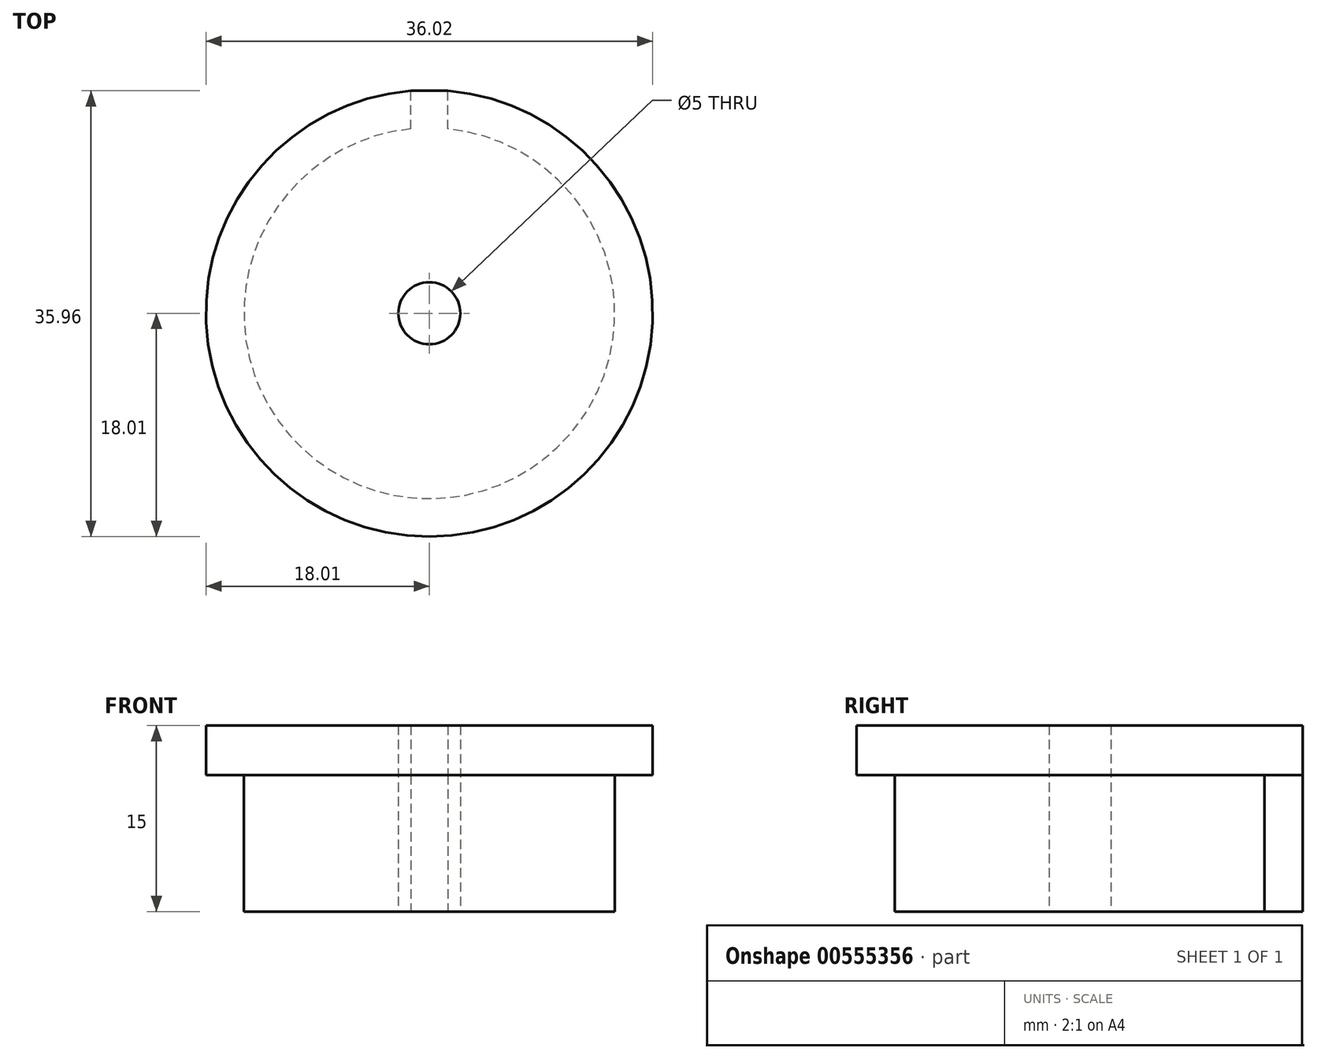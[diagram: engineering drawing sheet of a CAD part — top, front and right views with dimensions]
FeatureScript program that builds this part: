
annotation { "Feature Type Name" : "Feature", "Feature Type Description" : "" }
export const myFeature = defineFeature(function(context is Context, id is Id, definition is map)
    precondition{}
    {
        {
            var Q0;
            Q0=qCreatedBy(makeId("Top.planeOp"),FACE);
            var sketch = newSketch(context, id + "F0", { "sketchPlane" : qUnion([Q0])});
            skArc(sketch, "E0", {"start": v(-1.5, 14.87) * mm, "mid": v(0, -14.95) * mm, "end": v(1.5, 14.87) * mm});
            skLineSegment(sketch, "E1.top", {"start": v(1.5, 17.95) * mm, "end": v(-1.5, 17.95) * mm});
            skLineSegment(sketch, "E1.left", {"start": v(1.5, 14.87) * mm, "end": v(1.5, 17.95) * mm});
            skLineSegment(sketch, "E1.right", {"start": v(-1.5, 14.87) * mm, "end": v(-1.5, 17.95) * mm});
            skPoint(sketch, "E1.middle", {"position": v(0, 14.95) * mm});
            skPoint(sketch, "E2.orphan", {"position": v(-1.5, 11.95) * mm});
            skPoint(sketch, "E3.orphan", {"position": v(1.5, 11.95) * mm});
            skSolve(sketch);
        }
        {
            var Q0;
            Q0=qSketchRegion(id+"F0",true);
            extrude(context, id + "F1", {"entities" : qUnion([Q0]), "depth" : 11 * mm, "offsetDistance" : 25 * mm});
        }
        {
            var Q0;
            Q0=makeQuery(id+"F1.opExtrude","CAP_FACE",FACE,{"disambiguationData":[OSD([sQuery(id+"F0.wireOp",EDGE,"E0"),sQuery(id+"F0.wireOp",EDGE,"E1.top"),sQuery(id+"F0.wireOp",EDGE,"E1.left"),sQuery(id+"F0.wireOp",EDGE,"E1.right")])],"isStart":false});
            var sketch = newSketch(context, id + "F2", { "sketchPlane" : qUnion([Q0])});
            skCircle(sketch, "E4", {"center": v(0, 0) * mm, "radius": 18.01 * mm});
            skSolve(sketch);
        }
        {
            var Q0;
            Q0=makeQuery(id+"F2.imprint","IMPRINT",FACE,{"disambiguationData":[TD([[makeQuery(id+"F2.imprint","IMPRINT",EDGE,{"derivedFrom":makeQuery(id+"F1.opExtrude","CAP_EDGE",EDGE,{"disambiguationData":[OSD([sQuery(id+"F0.wireOp",EDGE,"E0")])],"isStart":false})}),-1.0]])]});
            var Q1;
            Q1=makeQuery(id+"F2.imprint","IMPRINT",FACE,{"disambiguationData":[TD([[makeQuery(id+"F2.imprint","IMPRINT",EDGE,{"derivedFrom":makeQuery(id+"F1.opExtrude","CAP_EDGE",EDGE,{"disambiguationData":[OSD([sQuery(id+"F0.wireOp",EDGE,"E0")])],"isStart":false})}),1.0]])]});
            extrude(context, id + "F3", {"entities" : qUnion([Q0, Q1]), "operationType" : NewBodyOperationType.ADD, "depth" : 4 * mm, "offsetDistance" : 25 * mm});
        }
        {
            var Q0;
            Q0=makeQuery(id+"F1.opExtrude","CAP_FACE",FACE,{"disambiguationData":[OSD([sQuery(id+"F0.wireOp",EDGE,"E0"),sQuery(id+"F0.wireOp",EDGE,"E1.top"),sQuery(id+"F0.wireOp",EDGE,"E1.left"),sQuery(id+"F0.wireOp",EDGE,"E1.right")])],"isStart":true});
            var sketch = newSketch(context, id + "F4", { "sketchPlane" : qUnion([Q0])});
            skPoint(sketch, "E5", {"position": v(0, 0) * mm});
            skSolve(sketch);
        }
        {
            var Q0;
            Q0=sQuery(id+"F4.wireOp",VERTEX,"E5");
            var Q1;
            Q1=makeQuery(id+"F1.opExtrude","SWEPT_BODY",BODY,{"disambiguationData":[OSD([sQuery(id+"F0.wireOp",EDGE,"E0"),sQuery(id+"F0.wireOp",EDGE,"E1.top"),sQuery(id+"F0.wireOp",EDGE,"E1.left"),sQuery(id+"F0.wireOp",EDGE,"E1.right")])]});
            hole(context, id + "F5", {"style" : HoleStyle.SIMPLE, "endStyle" : HoleEndStyle.THROUGH, "holeDiameter" : 5 * mm, "majorDiameter" : 5 * mm, "isTappedThrough" : true, "tappedDepth" : 12 * mm, "tapClearance" : 3, "locations" : qUnion([Q0]), "scope" : qUnion([Q1])});
        }
    });
